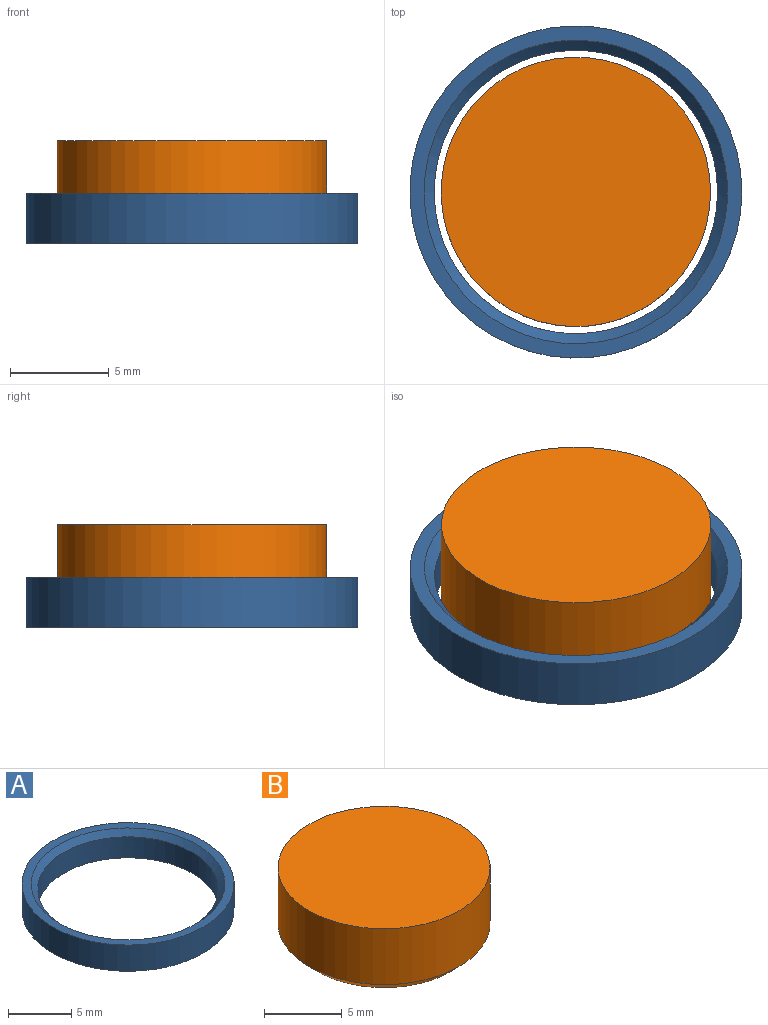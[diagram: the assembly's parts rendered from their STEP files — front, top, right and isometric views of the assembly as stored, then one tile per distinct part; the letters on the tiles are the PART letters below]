
ASSEMBLY  parts=2 mates=1
PART A: 5 faces, bbox 16.8x16.8x2.5 mm
  f0: cylinder r=8.41mm len=16.82mm, axis (0,0,1), area 134.2mm2, adj f1,f3
  f1: plane 16.82x16.82mm, normal (0,0,-1), area 60.3mm2, adj f0,f2
  f2: cylinder r=7.18mm len=14.35mm, axis (0,0,1), area 91.6mm2, adj f1,f4
  f3: plane 16.82x16.82mm, normal (0,0,1), area 36.6mm2, adj f0,f4
  f4: cone r=7.18mm half-angle=45deg, axis (0,0,1), area 33.5mm2, adj f2,f3
PART B: 4 faces, bbox 13.6x13.6x5.2 mm
  f0: cylinder r=6.82mm len=13.64mm, axis (0,0,-1), area 188.3mm2, adj f1,f3
  f1: plane 13.64x13.64mm, normal (0,0,1), area 146.1mm2, adj f0
  f2: plane 12.01x12.01mm, normal (0,0,-1), area 113.4mm2, adj f3
  f3: cone r=6.82mm half-angle=45deg, axis (0,0,1), area 46.3mm2, adj f0,f2
PLACE A at identity
PLACE B at identity
MATE fastened B.f0 <-> A.f0  axis (0,0,-1) through (0,0,0)mm
